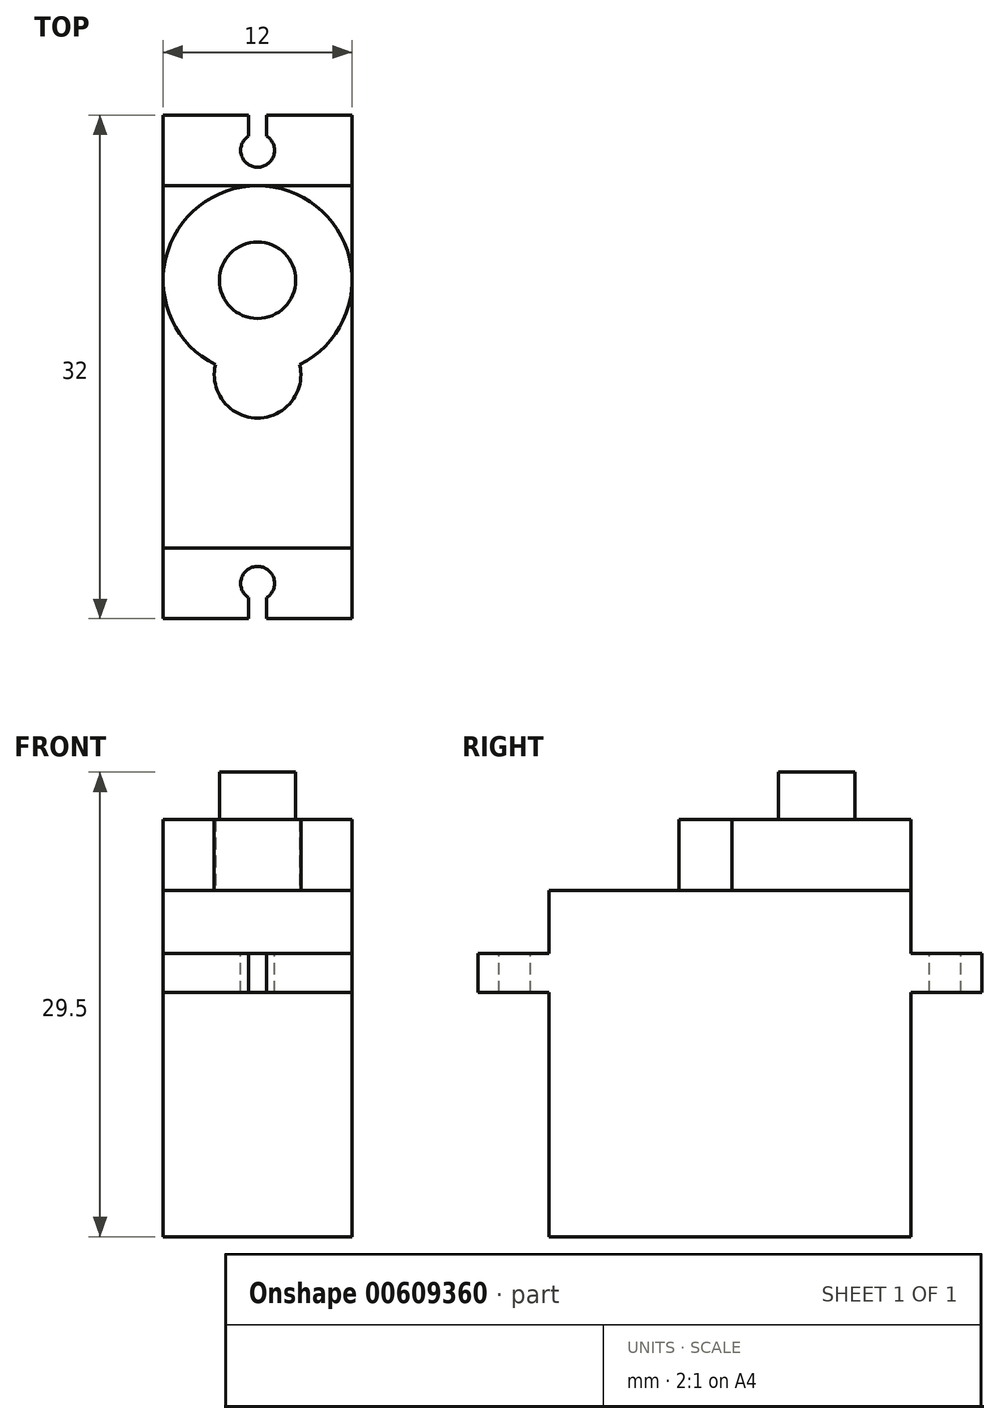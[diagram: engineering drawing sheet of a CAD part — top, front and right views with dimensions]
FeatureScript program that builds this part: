
annotation { "Feature Type Name" : "Feature", "Feature Type Description" : "" }
export const myFeature = defineFeature(function(context is Context, id is Id, definition is map)
    precondition{}
    {
        {
            var Q0;
            Q0=qCreatedBy(makeId("Top.planeOp"),FACE);
            var sketch = newSketch(context, id + "F0", { "sketchPlane" : qUnion([Q0])});
            skLineSegment(sketch, "E0.bottom", {"start": v(0, 0) * mm, "end": v(12, 0) * mm});
            skLineSegment(sketch, "E0.top", {"start": v(0, 23) * mm, "end": v(12, 23) * mm});
            skLineSegment(sketch, "E0.left", {"start": v(0, 0) * mm, "end": v(0, 23) * mm});
            skLineSegment(sketch, "E0.right", {"start": v(12, 0) * mm, "end": v(12, 23) * mm});
            skSolve(sketch);
        }
        {
            var Q0;
            Q0=qSketchRegion(id+"F0",true);
            extrude(context, id + "F1", {"entities" : qUnion([Q0]), "depth" : 22 * mm, "offsetDistance" : 25 * mm});
        }
        {
            var Q0;
            Q0=qCreatedBy(makeId("Top.planeOp"),FACE);
            cPlane(context, id + "F2", {"entities" : qUnion([Q0]), "cplaneType" : CPlaneType.OFFSET, "offset" : 15.5 * mm, "width" : 150 * mm, "height" : 150 * mm});
        }
        {
            var Q0;
            Q0=qCreatedBy(id+"F2.planeOp",FACE);
            var sketch = newSketch(context, id + "F3", { "sketchPlane" : qUnion([Q0])});
            skLineSegment(sketch, "E1.0", {"start": v(0, 23) * mm, "end": v(12, 23) * mm});
            skPoint(sketch, "E2.0", {"position": v(0, 11.5) * mm});
            skPoint(sketch, "E3.0", {"position": v(12, 11.5) * mm});
            skLineSegment(sketch, "E4", {"start": v(0, 11.5) * mm, "end": v(12, 11.5) * mm, "construction": true});
            skLineSegment(sketch, "E5", {"start": v(0, 23) * mm, "end": v(0, 27.5) * mm});
            skLineSegment(sketch, "E6", {"start": v(0, 27.5) * mm, "end": v(12, 27.5) * mm});
            skLineSegment(sketch, "E7", {"start": v(12, 27.5) * mm, "end": v(12, 23) * mm});
            skLineSegment(sketch, "E8.MirrorCS", {"start": v(0, 0) * mm, "end": v(12, 0) * mm});
            skLineSegment(sketch, "E9.MirrorCS", {"start": v(0, 0) * mm, "end": v(0, -4.5) * mm});
            skLineSegment(sketch, "E10.MirrorCS", {"start": v(0, -4.5) * mm, "end": v(12, -4.5) * mm});
            skLineSegment(sketch, "E11.MirrorCS", {"start": v(12, -4.5) * mm, "end": v(12, 0) * mm});
            skSolve(sketch);
        }
        {
            var Q0;
            Q0=qSketchRegion(id+"F3",true);
            extrude(context, id + "F4", {"entities" : qUnion([Q0]), "operationType" : NewBodyOperationType.ADD, "depth" : 2.5 * mm, "offsetDistance" : 25 * mm});
        }
        {
            var Q0;
            Q0=makeQuery(id+"F4.opExtrude","CAP_FACE",FACE,{"disambiguationData":[OSD([sQuery(id+"F3.wireOp",EDGE,"E1.0"),sQuery(id+"F3.wireOp",EDGE,"E5"),sQuery(id+"F3.wireOp",EDGE,"E6"),sQuery(id+"F3.wireOp",EDGE,"E7")])],"isStart":false});
            var sketch = newSketch(context, id + "F5", { "sketchPlane" : qUnion([Q0])});
            skCircle(sketch, "E12", {"center": v(6, 25.25) * mm, "radius": 1.07 * mm});
            skPoint(sketch, "E12.centerSnap0", {"position": v(12, 25.25) * mm});
            skPoint(sketch, "E12.centerSnap1", {"position": v(6, 27.5) * mm});
            skLineSegment(sketch, "E13", {"start": v(6, 27.5) * mm, "end": v(6, 25.25) * mm, "construction": true});
            skLineSegment(sketch, "E14", {"start": v(5.42, 27.5) * mm, "end": v(5.42, 26.16) * mm});
            skLineSegment(sketch, "E15", {"start": v(6.58, 27.5) * mm, "end": v(6.58, 26.16) * mm});
            skLineSegment(sketch, "E16", {"start": v(5.42, 27.5) * mm, "end": v(6, 27.5) * mm, "construction": true});
            skLineSegment(sketch, "E17", {"start": v(6, 27.5) * mm, "end": v(6.58, 27.5) * mm, "construction": true});
            skLineSegment(sketch, "E18.0.0", {"start": v(12, 23) * mm, "end": v(0, 23) * mm, "construction": true});
            skLineSegment(sketch, "E18.0.1", {"start": v(0, 23) * mm, "end": v(0, 0) * mm, "construction": true});
            skLineSegment(sketch, "E18.0.2", {"start": v(0, 0) * mm, "end": v(12, 0) * mm, "construction": true});
            skLineSegment(sketch, "E18.0.3", {"start": v(12, 0) * mm, "end": v(12, 23) * mm, "construction": true});
            skLineSegment(sketch, "E19", {"start": v(0, 11.5) * mm, "end": v(12, 11.5) * mm, "construction": true});
            skLineSegment(sketch, "E20.MirrorCS", {"start": v(6.58, -4.5) * mm, "end": v(6.58, -3.16) * mm});
            skCircle(sketch, "E21.MirrorC", {"center": v(6, -2.25) * mm, "radius": 1.07 * mm});
            skLineSegment(sketch, "E22.MirrorCS", {"start": v(6, -4.5) * mm, "end": v(6, -2.25) * mm, "construction": true});
            skPoint(sketch, "E23.MirrorP", {"position": v(6, -4.5) * mm});
            skLineSegment(sketch, "E24.MirrorCS", {"start": v(5.42, -4.5) * mm, "end": v(5.42, -3.16) * mm});
            skLineSegment(sketch, "E25", {"start": v(5.42, 27.5) * mm, "end": v(6.58, 27.5) * mm});
            skLineSegment(sketch, "E26.MirrorCS", {"start": v(5.42, -4.5) * mm, "end": v(6.58, -4.5) * mm});
            skLineSegment(sketch, "E27.MirrorCS", {"start": v(5.42, -4.5) * mm, "end": v(6, -4.5) * mm, "construction": true});
            skLineSegment(sketch, "E28.MirrorCS", {"start": v(6, -4.5) * mm, "end": v(6.58, -4.5) * mm, "construction": true});
            skSolve(sketch);
        }
        {
            var Q0;
            Q0=qSketchRegion(id+"F5",true);
            extrude(context, id + "F6", {"entities" : qUnion([Q0]), "operationType" : NewBodyOperationType.REMOVE, "endBound" : BoundingType.THROUGH_ALL, "oppositeDirection" : true, "depth" : 25 * mm, "offsetDistance" : 25 * mm});
        }
        {
            var Q0;
            Q0=makeQuery(id+"F1.opExtrude","CAP_FACE",FACE,{"disambiguationData":[OSD([sQuery(id+"F0.wireOp",EDGE,"E0.bottom"),sQuery(id+"F0.wireOp",EDGE,"E0.top"),sQuery(id+"F0.wireOp",EDGE,"E0.left"),sQuery(id+"F0.wireOp",EDGE,"E0.right")])],"isStart":false});
            var sketch = newSketch(context, id + "F7", { "sketchPlane" : qUnion([Q0])});
            skCircle(sketch, "E29", {"center": v(6, 17) * mm, "radius": 6 * mm});
            skPoint(sketch, "E29.centerSnap0", {"position": v(6, 23) * mm});
            skArc(sketch, "E30", {"start": v(3.32, 11.63) * mm, "mid": v(6, 8.25) * mm, "end": v(8.68, 11.63) * mm});
            skSolve(sketch);
        }
        {
            var Q0;
            Q0=qSketchRegion(id+"F7",true);
            extrude(context, id + "F8", {"entities" : qUnion([Q0]), "operationType" : NewBodyOperationType.ADD, "depth" : 4.5 * mm, "offsetDistance" : 25 * mm});
        }
        {
            var Q0;
            Q0=makeQuery(id+"F8.opExtrude","CAP_FACE",FACE,{"disambiguationData":[OSD([sQuery(id+"F7.wireOp",EDGE,"E29"),sQuery(id+"F7.wireOp",EDGE,"E30")])],"isStart":false});
            var sketch = newSketch(context, id + "F9", { "sketchPlane" : qUnion([Q0])});
            skCircle(sketch, "E31", {"center": v(6, 17) * mm, "radius": 2.43 * mm});
            skSolve(sketch);
        }
        {
            var Q0;
            Q0=qSketchRegion(id+"F9",true);
            extrude(context, id + "F10", {"entities" : qUnion([Q0]), "operationType" : NewBodyOperationType.ADD, "depth" : 3 * mm, "offsetDistance" : 25 * mm});
        }
    });
